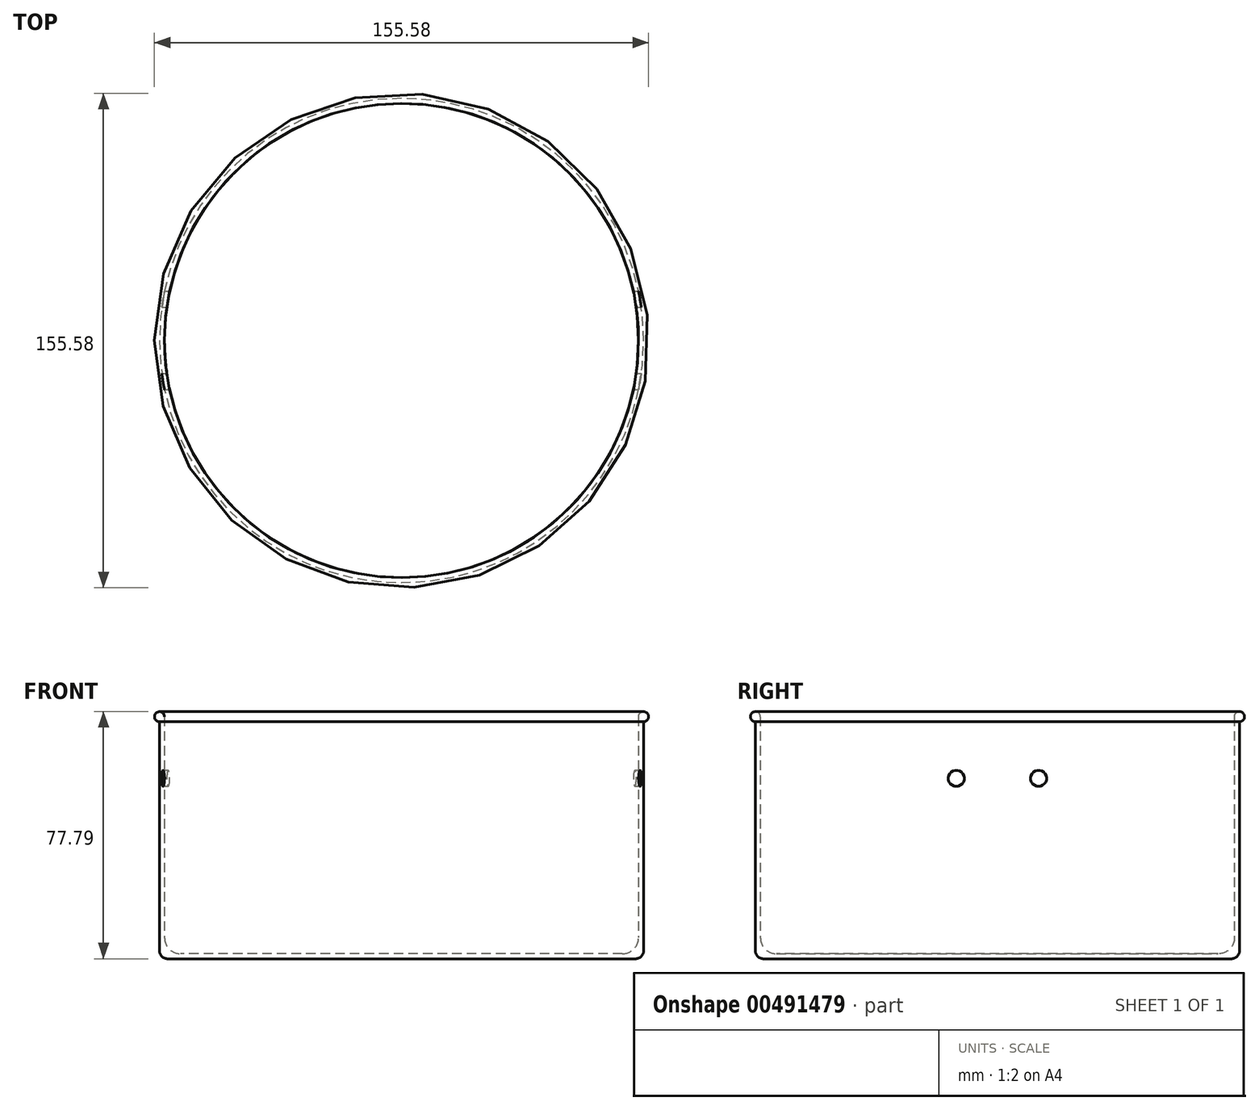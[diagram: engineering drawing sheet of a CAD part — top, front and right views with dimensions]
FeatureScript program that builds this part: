
annotation { "Feature Type Name" : "Feature", "Feature Type Description" : "" }
export const myFeature = defineFeature(function(context is Context, id is Id, definition is map)
    precondition{}
    {
        {
            var Q0;
            Q0=qCreatedBy(makeId("Front.planeOp"),FACE);
            var sketch = newSketch(context, id + "F0", { "sketchPlane" : qUnion([Q0])});
            skLineSegment(sketch, "E0", {"start": v(0, 0) * mm, "end": v(76.2, 0) * mm});
            skLineSegment(sketch, "E1", {"start": v(76.2, 0) * mm, "end": v(76.2, 74.61) * mm});
            skLineSegment(sketch, "E2", {"start": v(74.61, 76.2) * mm, "end": v(74.61, 1.59) * mm});
            skLineSegment(sketch, "E3", {"start": v(74.61, 1.59) * mm, "end": v(0, 1.59) * mm});
            skLineSegment(sketch, "E4", {"start": v(0, 1.59) * mm, "end": v(0, 0) * mm});
            skLineSegment(sketch, "E5.bottom", {"start": v(0, 0) * mm, "end": v(69.85, 0) * mm});
            skLineSegment(sketch, "E5.top", {"start": v(0, -1.59) * mm, "end": v(69.85, -1.59) * mm});
            skLineSegment(sketch, "E5.left", {"start": v(0, 0) * mm, "end": v(0, -1.59) * mm});
            skLineSegment(sketch, "E5.right", {"start": v(69.85, 0) * mm, "end": v(69.85, -1.59) * mm});
            skCircle(sketch, "E6", {"center": v(76.2, 76.2) * mm, "radius": 1.59 * mm});
            skLineSegment(sketch, "E7", {"start": v(0, 0) * mm, "end": v(0, 24.1) * mm, "construction": true});
            skSolve(sketch);
        }
        {
            var Q0;
            Q0=makeQuery(id+"F0.imprint","IMPRINT",FACE,{"disambiguationData":[TD([[makeQuery(id+"F0.imprint","IMPRINT",EDGE,{"derivedFrom":sQuery(id+"F0.wireOp",EDGE,"E0")}),1.0]])]});
            var Q1;
            Q1=makeQuery(id+"F0.imprint","IMPRINT",FACE,{"disambiguationData":[TD([[makeQuery(id+"F0.imprint","IMPRINT",EDGE,{"derivedFrom":sQuery(id+"F0.wireOp",EDGE,"E5.bottom")}),-1.0]])]});
            var Q2;
            {var subQ0=sQuery(id+"F0.wireOp",EDGE,"E6");var subQ1=makeQuery(id+"F0.imprint","INTERSECT",VERTEX,{"derivedFrom":[sQuery(id+"F0.wireOp",EDGE,"E1"),subQ0]});Q2=makeQuery(id+"F0.imprint","IMPRINT",FACE,{"disambiguationData":[TD([[makeQuery(id+"F0.imprint","IMPRINT",EDGE,{"disambiguationData":[TD([[subQ1,1.0]])],"derivedFrom":subQ0}),1.0]])]});}
            var Q3;
            Q3=sQuery(id+"F0.wireOp",EDGE,"E7");
            revolve(context, id + "F1", {"entities" : qUnion([Q0, Q1, Q2]), "axis" : qUnion([Q3]), "revolveType" : RevolveType.FULL});
        }
        {
            var Q0;
            Q0=makeQuery(id+"F1.opRevolve","SWEPT_EDGE",EDGE,{"disambiguationData":[OSD([sQuery(id+"F0.wireOp",EDGE,"E2"),sQuery(id+"F0.wireOp",EDGE,"E3")])]});
            fillet(context, id + "F2", {"entities" : qUnion([Q0]), "radius" : 5.08 * mm, "tangentPropagation" : true, "allowEdgeOverflow" : false});
        }
        {
            var Q0;
            Q0=makeQuery(id+"F1.opRevolve","SWEPT_EDGE",EDGE,{"disambiguationData":[OSD([sQuery(id+"F0.wireOp",EDGE,"E0"),sQuery(id+"F0.wireOp",EDGE,"E1")])]});
            fillet(context, id + "F3", {"entities" : qUnion([Q0]), "radius" : 2.54 * mm, "tangentPropagation" : true, "allowEdgeOverflow" : false});
        }
        {
            var Q0;
            Q0=qCreatedBy(makeId("Right.planeOp"),FACE);
            cPlane(context, id + "F4", {"entities" : qUnion([Q0]), "cplaneType" : CPlaneType.OFFSET, "offset" : 101.6 * mm, "width" : 152.4 * mm, "height" : 152.4 * mm});
        }
        {
            var Q0;
            Q0=qCreatedBy(id+"F4.planeOp",FACE);
            var sketch = newSketch(context, id + "F5", { "sketchPlane" : qUnion([Q0])});
            skCircle(sketch, "E8", {"center": v(-12.95, 56.8) * mm, "radius": 2.54 * mm});
            skCircle(sketch, "E9", {"center": v(12.95, 56.8) * mm, "radius": 2.54 * mm});
            skLineSegment(sketch, "E10", {"start": v(0, 0) * mm, "end": v(0, 77.12) * mm, "construction": true});
            skSolve(sketch);
        }
        {
            var Q0;
            Q0=makeQuery(id+"F5.imprint","IMPRINT",FACE,{"disambiguationData":[TD([[makeQuery(id+"F5.imprint","IMPRINT",EDGE,{"derivedFrom":sQuery(id+"F5.wireOp",EDGE,"E8")}),1.0]])]});
            extrude(context, id + "F6", {"entities" : qUnion([Q0]), "operationType" : NewBodyOperationType.REMOVE, "oppositeDirection" : true, "depth" : 228.85 * mm});
        }
        {
            var Q0;
            Q0=makeQuery(id+"F5.imprint","IMPRINT",FACE,{"disambiguationData":[TD([[makeQuery(id+"F5.imprint","IMPRINT",EDGE,{"derivedFrom":sQuery(id+"F5.wireOp",EDGE,"E9")}),1.0]])]});
            extrude(context, id + "F7", {"entities" : qUnion([Q0]), "operationType" : NewBodyOperationType.REMOVE, "oppositeDirection" : true, "depth" : 243.84 * mm});
        }
    });
